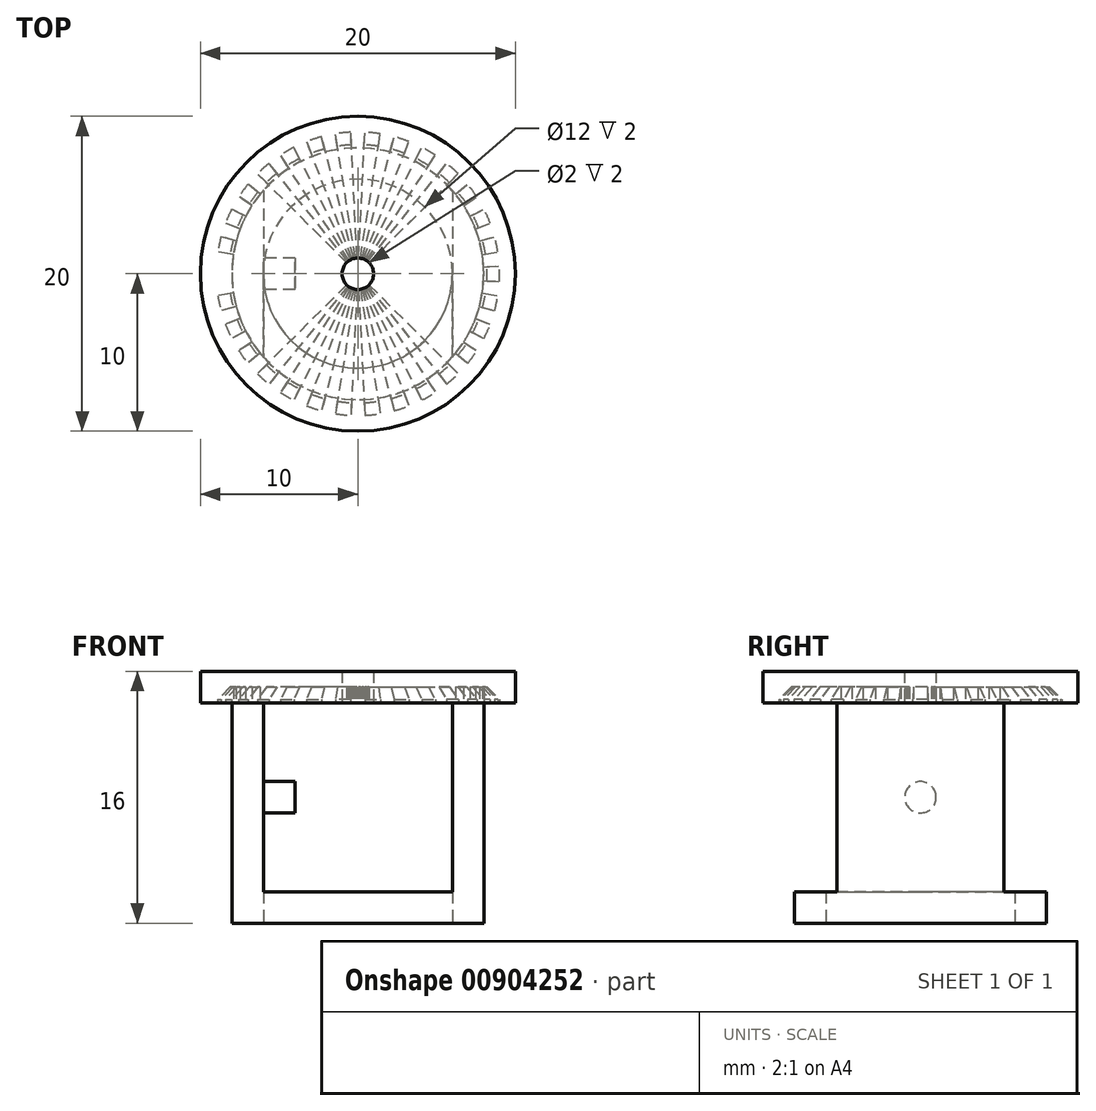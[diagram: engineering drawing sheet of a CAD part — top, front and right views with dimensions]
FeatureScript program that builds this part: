
annotation { "Feature Type Name" : "Feature", "Feature Type Description" : "" }
export const myFeature = defineFeature(function(context is Context, id is Id, definition is map)
    precondition{}
    {
        {
            var Q0;
            Q0=qCreatedBy(makeId("Front.planeOp"),FACE);
            var sketch = newSketch(context, id + "F0", { "sketchPlane" : qUnion([Q0])});
            skLineSegment(sketch, "E0.bottom", {"start": v(0, 0) * mm, "end": v(-5, 0) * mm});
            skLineSegment(sketch, "E0.top", {"start": v(0, 2) * mm, "end": v(-5, 2) * mm});
            skLineSegment(sketch, "E0.left", {"start": v(0, 0) * mm, "end": v(0, 2) * mm});
            skLineSegment(sketch, "E0.right", {"start": v(-5, 0) * mm, "end": v(-5, 2) * mm});
            skLineSegment(sketch, "E1.bottom", {"start": v(-5, 2) * mm, "end": v(-4, 2) * mm});
            skLineSegment(sketch, "E1.top", {"start": v(-5, 1) * mm, "end": v(-4, 1) * mm});
            skLineSegment(sketch, "E1.left", {"start": v(-5, 2) * mm, "end": v(-5, 1) * mm});
            skLineSegment(sketch, "E1.right", {"start": v(-4, 2) * mm, "end": v(-4, 1) * mm});
            skLineSegment(sketch, "E2.bottom", {"start": v(-4, 1) * mm, "end": v(-6, 1) * mm});
            skLineSegment(sketch, "E2.top", {"start": v(-4, 11) * mm, "end": v(-6, 11) * mm});
            skLineSegment(sketch, "E2.left", {"start": v(-4, 1) * mm, "end": v(-4, 11) * mm});
            skLineSegment(sketch, "E2.right", {"start": v(-6, 1) * mm, "end": v(-6, 11) * mm});
            skLineSegment(sketch, "E3", {"start": v(-1, 2) * mm, "end": v(-1, 0) * mm});
            skLineSegment(sketch, "E4.bottom", {"start": v(-6, 1) * mm, "end": v(-5, 1) * mm});
            skLineSegment(sketch, "E4.top", {"start": v(-6, 0) * mm, "end": v(-5, 0) * mm});
            skLineSegment(sketch, "E4.left", {"start": v(-6, 1) * mm, "end": v(-6, 0) * mm});
            skLineSegment(sketch, "E4.right", {"start": v(-5, 1) * mm, "end": v(-5, 0) * mm});
            skLineSegment(sketch, "E5.bottom", {"start": v(0, 0) * mm, "end": v(-6, 0) * mm});
            skLineSegment(sketch, "E5.top", {"start": v(0, -2) * mm, "end": v(-6, -2) * mm});
            skLineSegment(sketch, "E5.left", {"start": v(0, 0) * mm, "end": v(0, -2) * mm});
            skLineSegment(sketch, "E5.right", {"start": v(-6, 0) * mm, "end": v(-6, -2) * mm});
            skLineSegment(sketch, "E6.bottom", {"start": v(0, -2) * mm, "end": v(0, -2) * mm});
            skLineSegment(sketch, "E6.top", {"start": v(0, 0) * mm, "end": v(0, 0) * mm});
            skLineSegment(sketch, "E6.left", {"start": v(0, -2) * mm, "end": v(0, 0) * mm});
            skLineSegment(sketch, "E6.right", {"start": v(0, -2) * mm, "end": v(0, 0) * mm});
            skLineSegment(sketch, "E7.bottom", {"start": v(-6, -2) * mm, "end": v(-8, -2) * mm});
            skLineSegment(sketch, "E7.top", {"start": v(-6, 11) * mm, "end": v(-8, 11) * mm});
            skLineSegment(sketch, "E7.left", {"start": v(-6, -2) * mm, "end": v(-6, 11) * mm});
            skLineSegment(sketch, "E7.right", {"start": v(-8, -2) * mm, "end": v(-8, 11) * mm});
            skLineSegment(sketch, "E8.bottom", {"start": v(-4, 11) * mm, "end": v(-5, 11) * mm});
            skLineSegment(sketch, "E8.top", {"start": v(-4, 10) * mm, "end": v(-5, 10) * mm});
            skLineSegment(sketch, "E8.left", {"start": v(-4, 11) * mm, "end": v(-4, 10) * mm});
            skLineSegment(sketch, "E8.right", {"start": v(-5, 11) * mm, "end": v(-5, 10) * mm});
            skLineSegment(sketch, "E9.bottom", {"start": v(-5, 10) * mm, "end": v(0, 10) * mm});
            skLineSegment(sketch, "E9.top", {"start": v(-5, 12) * mm, "end": v(0, 12) * mm});
            skLineSegment(sketch, "E9.left", {"start": v(-5, 10) * mm, "end": v(-5, 12) * mm});
            skLineSegment(sketch, "E9.right", {"start": v(0, 10) * mm, "end": v(0, 12) * mm});
            skLineSegment(sketch, "E10.bottom", {"start": v(-8, 11) * mm, "end": v(-5, 11) * mm});
            skLineSegment(sketch, "E10.top", {"start": v(-8, 12) * mm, "end": v(-5, 12) * mm});
            skLineSegment(sketch, "E10.left", {"start": v(-8, 11) * mm, "end": v(-8, 12) * mm});
            skLineSegment(sketch, "E10.right", {"start": v(-5, 11) * mm, "end": v(-5, 12) * mm});
            skLineSegment(sketch, "E11", {"start": v(-6, 11) * mm, "end": v(-6, 12) * mm});
            skLineSegment(sketch, "E12.bottom", {"start": v(0, 12) * mm, "end": v(-8, 12) * mm});
            skLineSegment(sketch, "E12.top", {"start": v(0, 14) * mm, "end": v(-8, 14) * mm});
            skLineSegment(sketch, "E12.left", {"start": v(0, 12) * mm, "end": v(0, 14) * mm});
            skLineSegment(sketch, "E12.right", {"start": v(-8, 12) * mm, "end": v(-8, 14) * mm});
            skLineSegment(sketch, "E13", {"start": v(-1, 0) * mm, "end": v(-1, -2) * mm});
            skLineSegment(sketch, "E14", {"start": v(-1, -2) * mm, "end": v(-1, 14) * mm});
            skLineSegment(sketch, "E15.bottom", {"start": v(-8, 12) * mm, "end": v(-10, 12) * mm});
            skLineSegment(sketch, "E15.top", {"start": v(-8, 14) * mm, "end": v(-10, 14) * mm});
            skLineSegment(sketch, "E15.right", {"start": v(-10, 12) * mm, "end": v(-10, 14) * mm});
            skSolve(sketch);
        }
        {
            var Q0;
            {var subQ5=sQuery(id+"F0.wireOp",EDGE,"E7.bottom");Q0=makeQuery(id+"F0.imprint","IMPRINT",FACE,{"disambiguationData":[TD([[makeQuery(id+"F0.imprint","IMPRINT",EDGE,{"derivedFrom":subQ5}),-1.0]])]});}
            var Q1;
            {var subQ5=sQuery(id+"F0.wireOp",EDGE,"E5.bottom");var subQ7=makeQuery(id+"F0.imprint","INTERSECT",VERTEX,{"derivedFrom":[sQuery(id+"F0.wireOp",EDGE,"E4.right"),subQ5]});Q1=makeQuery(id+"F0.imprint","IMPRINT",FACE,{"disambiguationData":[TD([[makeQuery(id+"F0.imprint","IMPRINT",EDGE,{"disambiguationData":[TD([[subQ7,1.0]])],"derivedFrom":subQ5}),1.0]])]});}
            var Q2;
            {var subQ0=sQuery(id+"F0.wireOp",EDGE,"E12.right");Q2=makeQuery(id+"F0.imprint","IMPRINT",FACE,{"disambiguationData":[TD([[makeQuery(id+"F0.imprint","IMPRINT",EDGE,{"derivedFrom":subQ0}),-1.0]])]});}
            var Q3;
            Q3=makeQuery(id+"F0.imprint","IMPRINT",FACE,{"disambiguationData":[TD([[makeQuery(id+"F0.imprint","IMPRINT",EDGE,{"derivedFrom":sQuery(id+"F0.wireOp",EDGE,"E15.bottom")}),-1.0]])]});
            var Q4;
            {var subQ2=sQuery(id+"F0.wireOp",EDGE,"E10.left");Q4=makeQuery(id+"F0.imprint","IMPRINT",FACE,{"disambiguationData":[TD([[makeQuery(id+"F0.imprint","IMPRINT",EDGE,{"derivedFrom":subQ2}),-1.0]])]});}
            var Q5;
            Q5=sQuery(id+"F0.wireOp",EDGE,"E9.right");
            revolve(context, id + "F1", {"surfaceOperationType" : NewSurfaceOperationType.NEW, "entities" : qUnion([Q0, Q1, Q2, Q3, Q4]), "axis" : qUnion([Q5]), "revolveType" : RevolveType.FULL});
        }
        {
            var Q0;
            Q0=qCreatedBy(makeId("Front.planeOp"),FACE);
            var sketch = newSketch(context, id + "F2", { "sketchPlane" : qUnion([Q0])});
            skLineSegment(sketch, "E16.0", {"start": v(6, 0) * mm, "end": v(-6, 0) * mm});
            skLineSegment(sketch, "E17.0", {"start": v(10, 12) * mm, "end": v(-10, 12) * mm});
            skLineSegment(sketch, "E18", {"start": v(-6, 0) * mm, "end": v(-6, 12) * mm});
            skLineSegment(sketch, "E19", {"start": v(6, 0) * mm, "end": v(6, 12) * mm});
            skSolve(sketch);
        }
        {
            var Q0;
            Q0=makeQuery(id+"F2.imprint","IMPRINT",FACE,{"disambiguationData":[TD([[makeQuery(id+"F2.imprint","IMPRINT",EDGE,{"derivedFrom":sQuery(id+"F2.wireOp",EDGE,"E16.0")}),-1.0]])]});
            extrude(context, id + "F3", {"entities" : qUnion([Q0]), "operationType" : NewBodyOperationType.REMOVE, "oppositeDirection" : true, "depth" : 25 * mm, "offsetDistance" : 25 * mm});
        }
        {
            var Q0;
            Q0=makeQuery(id+"F2.imprint","IMPRINT",FACE,{"disambiguationData":[TD([[makeQuery(id+"F2.imprint","IMPRINT",EDGE,{"derivedFrom":sQuery(id+"F2.wireOp",EDGE,"E16.0")}),-1.0]])]});
            extrude(context, id + "F4", {"entities" : qUnion([Q0]), "operationType" : NewBodyOperationType.REMOVE, "oppositeDirection" : true, "depth" : -25 * mm, "offsetDistance" : 25 * mm});
        }
        {
            var Q0;
            Q0=makeQuery(id+"F1.opRevolve","SWEPT_FACE",FACE,{"disambiguationData":[OSD([sQuery(id+"F0.wireOp",EDGE,"E12.top"),sQuery(id+"F0.wireOp",EDGE,"E15.top")])]});
            var sketch = newSketch(context, id + "F5", { "sketchPlane" : qUnion([Q0])});
            skLineSegment(sketch, "E20", {"start": v(-0.5, 9.99) * mm, "end": v(0.5, 9.99) * mm});
            skLineSegment(sketch, "E21", {"start": v(0, 0) * mm, "end": v(0.5, 9.99) * mm});
            skLineSegment(sketch, "E22", {"start": v(0, 0) * mm, "end": v(-0.5, 9.99) * mm});
            skCircle(sketch, "E23", {"center": v(0, 0) * mm, "radius": 9 * mm});
            skLineSegment(sketch, "E24", {"start": v(0, 0) * mm, "end": v(9, 0) * mm});
            skLineSegment(sketch, "E25", {"start": v(9, 0) * mm, "end": v(10, 0) * mm});
            skLineSegment(sketch, "E26.1.0", {"start": v(0, 0) * mm, "end": v(-2.57, 9.67) * mm});
            skLineSegment(sketch, "E26.1.1", {"start": v(0, 0) * mm, "end": v(-1.59, 9.87) * mm});
            skLineSegment(sketch, "E26.2.0", {"start": v(0, 0) * mm, "end": v(-4.52, 8.92) * mm});
            skLineSegment(sketch, "E26.2.1", {"start": v(0, 0) * mm, "end": v(-3.6, 9.33) * mm});
            skLineSegment(sketch, "E27.2.3.0", {"start": v(0, 0) * mm, "end": v(-6.28, 7.79) * mm});
            skLineSegment(sketch, "E27.3.3.0", {"start": v(0, 0) * mm, "end": v(-5.47, 8.37) * mm});
            skLineSegment(sketch, "E27.2.4.0", {"start": v(0, 0) * mm, "end": v(-7.76, 6.31) * mm});
            skLineSegment(sketch, "E27.3.4.0", {"start": v(0, 0) * mm, "end": v(-7.09, 7.05) * mm});
            skLineSegment(sketch, "E27.2.5.0", {"start": v(0, 0) * mm, "end": v(-8.9, 4.56) * mm});
            skLineSegment(sketch, "E27.3.5.0", {"start": v(0, 0) * mm, "end": v(-8.4, 5.43) * mm});
            skLineSegment(sketch, "E27.2.6.0", {"start": v(0, 0) * mm, "end": v(-9.65, 2.61) * mm});
            skLineSegment(sketch, "E27.3.6.0", {"start": v(0, 0) * mm, "end": v(-9.34, 3.56) * mm});
            skLineSegment(sketch, "E27.2.7.0", {"start": v(0, 0) * mm, "end": v(-9.99, 0.55) * mm});
            skLineSegment(sketch, "E27.3.7.0", {"start": v(0, 0) * mm, "end": v(-9.88, 1.54) * mm});
            skLineSegment(sketch, "E27.2.8.0", {"start": v(0, 0) * mm, "end": v(-9.88, -1.54) * mm});
            skLineSegment(sketch, "E27.3.8.0", {"start": v(0, 0) * mm, "end": v(-9.99, -0.55) * mm});
            skLineSegment(sketch, "E27.2.9.0", {"start": v(0, 0) * mm, "end": v(-9.34, -3.56) * mm});
            skLineSegment(sketch, "E27.3.9.0", {"start": v(0, 0) * mm, "end": v(-9.65, -2.61) * mm});
            skLineSegment(sketch, "E27.2.10.0", {"start": v(0, 0) * mm, "end": v(-8.4, -5.43) * mm});
            skLineSegment(sketch, "E27.3.10.0", {"start": v(0, 0) * mm, "end": v(-8.9, -4.56) * mm});
            skLineSegment(sketch, "E27.2.11.0", {"start": v(0, 0) * mm, "end": v(-7.09, -7.05) * mm});
            skLineSegment(sketch, "E27.3.11.0", {"start": v(0, 0) * mm, "end": v(-7.76, -6.31) * mm});
            skLineSegment(sketch, "E27.2.12.0", {"start": v(0, 0) * mm, "end": v(-5.47, -8.37) * mm});
            skLineSegment(sketch, "E27.3.12.0", {"start": v(0, 0) * mm, "end": v(-6.28, -7.79) * mm});
            skLineSegment(sketch, "E27.2.13.0", {"start": v(0, 0) * mm, "end": v(-3.6, -9.33) * mm});
            skLineSegment(sketch, "E27.3.13.0", {"start": v(0, 0) * mm, "end": v(-4.52, -8.92) * mm});
            skLineSegment(sketch, "E27.2.14.0", {"start": v(0, 0) * mm, "end": v(-1.59, -9.87) * mm});
            skLineSegment(sketch, "E27.3.14.0", {"start": v(0, 0) * mm, "end": v(-2.57, -9.67) * mm});
            skLineSegment(sketch, "E27.2.15.0", {"start": v(0, 0) * mm, "end": v(0.5, -9.99) * mm});
            skLineSegment(sketch, "E27.3.15.0", {"start": v(0, 0) * mm, "end": v(-0.5, -9.99) * mm});
            skLineSegment(sketch, "E27.2.16.0", {"start": v(0, 0) * mm, "end": v(2.57, -9.67) * mm});
            skLineSegment(sketch, "E27.3.16.0", {"start": v(0, 0) * mm, "end": v(1.59, -9.87) * mm});
            skLineSegment(sketch, "E27.2.17.0", {"start": v(0, 0) * mm, "end": v(4.52, -8.92) * mm});
            skLineSegment(sketch, "E27.3.17.0", {"start": v(0, 0) * mm, "end": v(3.6, -9.33) * mm});
            skLineSegment(sketch, "E27.2.18.0", {"start": v(0, 0) * mm, "end": v(6.28, -7.79) * mm});
            skLineSegment(sketch, "E27.3.18.0", {"start": v(0, 0) * mm, "end": v(5.47, -8.37) * mm});
            skLineSegment(sketch, "E27.2.19.0", {"start": v(0, 0) * mm, "end": v(7.76, -6.31) * mm});
            skLineSegment(sketch, "E27.3.19.0", {"start": v(0, 0) * mm, "end": v(7.09, -7.05) * mm});
            skLineSegment(sketch, "E27.2.20.0", {"start": v(0, 0) * mm, "end": v(8.9, -4.56) * mm});
            skLineSegment(sketch, "E27.3.20.0", {"start": v(0, 0) * mm, "end": v(8.4, -5.43) * mm});
            skLineSegment(sketch, "E27.2.21.0", {"start": v(0, 0) * mm, "end": v(9.65, -2.61) * mm});
            skLineSegment(sketch, "E27.3.21.0", {"start": v(0, 0) * mm, "end": v(9.34, -3.56) * mm});
            skLineSegment(sketch, "E27.2.22.0", {"start": v(0, 0) * mm, "end": v(9.99, -0.55) * mm});
            skLineSegment(sketch, "E27.3.22.0", {"start": v(0, 0) * mm, "end": v(9.88, -1.54) * mm});
            skLineSegment(sketch, "E27.2.23.0", {"start": v(0, 0) * mm, "end": v(9.88, 1.54) * mm});
            skLineSegment(sketch, "E27.3.23.0", {"start": v(0, 0) * mm, "end": v(9.99, 0.55) * mm});
            skLineSegment(sketch, "E27.2.24.0", {"start": v(0, 0) * mm, "end": v(9.34, 3.56) * mm});
            skLineSegment(sketch, "E27.3.24.0", {"start": v(0, 0) * mm, "end": v(9.65, 2.61) * mm});
            skLineSegment(sketch, "E28.2.25.0", {"start": v(0, 0) * mm, "end": v(8.4, 5.43) * mm});
            skLineSegment(sketch, "E28.3.25.0", {"start": v(0, 0) * mm, "end": v(8.9, 4.56) * mm});
            skLineSegment(sketch, "E29.2.26.0", {"start": v(0, 0) * mm, "end": v(7.09, 7.05) * mm});
            skLineSegment(sketch, "E29.3.26.0", {"start": v(0, 0) * mm, "end": v(7.76, 6.31) * mm});
            skLineSegment(sketch, "E29.2.27.0", {"start": v(0, 0) * mm, "end": v(5.47, 8.37) * mm});
            skLineSegment(sketch, "E29.3.27.0", {"start": v(0, 0) * mm, "end": v(6.28, 7.79) * mm});
            skLineSegment(sketch, "E29.2.28.0", {"start": v(0, 0) * mm, "end": v(3.6, 9.33) * mm});
            skLineSegment(sketch, "E29.3.28.0", {"start": v(0, 0) * mm, "end": v(4.52, 8.92) * mm});
            skLineSegment(sketch, "E29.2.29.0", {"start": v(0, 0) * mm, "end": v(1.59, 9.87) * mm});
            skLineSegment(sketch, "E29.3.29.0", {"start": v(0, 0) * mm, "end": v(2.57, 9.67) * mm});
            skSolve(sketch);
        }
        {
            var Q0;
            {var subQ0=sQuery(id+"F2.wireOp",EDGE,"E18");Q0=makeQuery(id+"F4.boolean.opBoolean","MERGE",FACE,{"derivedFrom":[makeQuery(id+"F3.boolean.opBoolean","COPY",FACE,{"derivedFrom":makeQuery(id+"F3.opExtrude","SWEPT_FACE",FACE,{"disambiguationData":[OSD([subQ0])]})})],"fromTools":[makeQuery(id+"F4.opExtrude","SWEPT_FACE",FACE,{"disambiguationData":[OSD([subQ0])]})]});}
            var sketch = newSketch(context, id + "F6", { "sketchPlane" : qUnion([Q0])});
            skLineSegment(sketch, "E30.0", {"start": v(10, 12) * mm, "end": v(-10, 12) * mm});
            skLineSegment(sketch, "E31.0", {"start": v(5.3, 0) * mm, "end": v(8, 0) * mm});
            skLineSegment(sketch, "E32.0", {"start": v(-5.3, 0) * mm, "end": v(-8, 0) * mm});
            skLineSegment(sketch, "E33", {"start": v(-5.3, 0) * mm, "end": v(5.3, 0) * mm});
            skLineSegment(sketch, "E34", {"start": v(0, 0) * mm, "end": v(0, 12) * mm});
            skLineSegment(sketch, "E35.0", {"start": v(-5.3, 12) * mm, "end": v(-5.3, 0) * mm});
            skLineSegment(sketch, "E36.0", {"start": v(5.3, 12) * mm, "end": v(5.3, 0) * mm});
            skLineSegment(sketch, "E37", {"start": v(-5.3, 6) * mm, "end": v(5.3, 6) * mm});
            skCircle(sketch, "E38", {"center": v(0, 6) * mm, "radius": 1 * mm});
            skSolve(sketch);
        }
        {
            var Q0;
            {var subQ0=sQuery(id+"F6.wireOp",EDGE,"E37");var subQ1=sQuery(id+"F6.wireOp",EDGE,"E34");var subQ2=makeQuery(id+"F6.imprint","INTERSECT",VERTEX,{"derivedFrom":[subQ1,subQ0]});Q0=makeQuery(id+"F6.imprint","IMPRINT",FACE,{"disambiguationData":[TD([[makeQuery(id+"F6.imprint","IMPRINT",EDGE,{"disambiguationData":[TD([[subQ2,-1.0]])],"derivedFrom":subQ1}),-1.0]])]});}
            var Q1;
            {var subQ0=sQuery(id+"F6.wireOp",EDGE,"E38");var subQ1=sQuery(id+"F6.wireOp",EDGE,"E34");var subQ2=makeQuery(id+"F6.imprint","INTERSECT",VERTEX,{"disambiguationData":[OD(0.0)],"derivedFrom":[subQ1,subQ0]});Q1=makeQuery(id+"F6.imprint","IMPRINT",FACE,{"disambiguationData":[TD([[makeQuery(id+"F6.imprint","IMPRINT",EDGE,{"disambiguationData":[TD([[subQ2,-1.0]])],"derivedFrom":subQ1}),-1.0]])]});}
            var Q2;
            {var subQ0=sQuery(id+"F6.wireOp",EDGE,"E38");var subQ1=sQuery(id+"F6.wireOp",EDGE,"E34");var subQ2=makeQuery(id+"F6.imprint","INTERSECT",VERTEX,{"disambiguationData":[OD(0.0)],"derivedFrom":[subQ1,subQ0]});Q2=makeQuery(id+"F6.imprint","IMPRINT",FACE,{"disambiguationData":[TD([[makeQuery(id+"F6.imprint","IMPRINT",EDGE,{"disambiguationData":[TD([[subQ2,-1.0]])],"derivedFrom":subQ1}),1.0]])]});}
            var Q3;
            {var subQ0=sQuery(id+"F6.wireOp",EDGE,"E37");var subQ1=sQuery(id+"F6.wireOp",EDGE,"E34");var subQ2=makeQuery(id+"F6.imprint","INTERSECT",VERTEX,{"derivedFrom":[subQ1,subQ0]});Q3=makeQuery(id+"F6.imprint","IMPRINT",FACE,{"disambiguationData":[TD([[makeQuery(id+"F6.imprint","IMPRINT",EDGE,{"disambiguationData":[TD([[subQ2,-1.0]])],"derivedFrom":subQ1}),1.0]])]});}
            extrude(context, id + "F7", {"entities" : qUnion([Q0, Q1, Q2, Q3]), "operationType" : NewBodyOperationType.ADD, "depth" : 2 * mm, "offsetDistance" : 25 * mm});
        }
        {
            var Q0;
            {var subQ0=sQuery(id+"F2.wireOp",EDGE,"E17.0");Q0=makeQuery(id+"F4.boolean.opBoolean","MERGE",FACE,{"derivedFrom":[makeQuery(id+"F3.boolean.opBoolean","MERGE",FACE,{"derivedFrom":[makeQuery(id+"F1.opRevolve","SWEPT_FACE",FACE,{"disambiguationData":[OSD([sQuery(id+"F0.wireOp",EDGE,"E12.bottom")])]}),makeQuery(id+"F1.opRevolve","SWEPT_FACE",FACE,{"disambiguationData":[OSD([sQuery(id+"F0.wireOp",EDGE,"E15.bottom")])]})],"fromTools":[makeQuery(id+"F3.opExtrude","SWEPT_FACE",FACE,{"disambiguationData":[OSD([subQ0])]})]})],"fromTools":[makeQuery(id+"F4.opExtrude","SWEPT_FACE",FACE,{"disambiguationData":[OSD([subQ0])]})]});}
            var sketch = newSketch(context, id + "F8", { "sketchPlane" : qUnion([Q0])});
            skCircle(sketch, "E39.0", {"center": v(0, 0) * mm, "radius": 9 * mm});
            skLineSegment(sketch, "E40.0", {"start": v(0, 0) * mm, "end": v(-7.76, 6.31) * mm});
            skLineSegment(sketch, "E41.0", {"start": v(0, 0) * mm, "end": v(-7.09, 7.05) * mm});
            skLineSegment(sketch, "E42.0", {"start": v(0, 0) * mm, "end": v(-6.28, 7.79) * mm});
            skLineSegment(sketch, "E43.0", {"start": v(0, 0) * mm, "end": v(-5.47, 8.37) * mm});
            skLineSegment(sketch, "E44.0", {"start": v(0, 0) * mm, "end": v(-4.52, 8.92) * mm});
            skLineSegment(sketch, "E45.0", {"start": v(0, 0) * mm, "end": v(-3.6, 9.33) * mm});
            skLineSegment(sketch, "E46.0", {"start": v(0, 0) * mm, "end": v(-2.57, 9.67) * mm});
            skLineSegment(sketch, "E47.0", {"start": v(0, 0) * mm, "end": v(-1.59, 9.87) * mm});
            skLineSegment(sketch, "E48.0", {"start": v(0, 0) * mm, "end": v(-0.5, 9.99) * mm});
            skLineSegment(sketch, "E49.0", {"start": v(0, 0) * mm, "end": v(0.5, 9.99) * mm});
            skLineSegment(sketch, "E50.0", {"start": v(0, 0) * mm, "end": v(1.59, 9.87) * mm});
            skLineSegment(sketch, "E51.0", {"start": v(0, 0) * mm, "end": v(2.57, 9.67) * mm});
            skLineSegment(sketch, "E52.0", {"start": v(0, 0) * mm, "end": v(3.6, 9.33) * mm});
            skLineSegment(sketch, "E53.0", {"start": v(0, 0) * mm, "end": v(4.52, 8.92) * mm});
            skLineSegment(sketch, "E54.0", {"start": v(0, 0) * mm, "end": v(5.47, 8.37) * mm});
            skLineSegment(sketch, "E55.0", {"start": v(0, 0) * mm, "end": v(6.28, 7.79) * mm});
            skLineSegment(sketch, "E56.0", {"start": v(0, 0) * mm, "end": v(7.09, 7.05) * mm});
            skLineSegment(sketch, "E57.0", {"start": v(0, 0) * mm, "end": v(7.76, 6.31) * mm});
            skLineSegment(sketch, "E58.0", {"start": v(0, 0) * mm, "end": v(8.4, 5.43) * mm});
            skLineSegment(sketch, "E59.0", {"start": v(0, 0) * mm, "end": v(8.9, 4.56) * mm});
            skLineSegment(sketch, "E60.0", {"start": v(0, 0) * mm, "end": v(9.34, 3.56) * mm});
            skLineSegment(sketch, "E61.0", {"start": v(0, 0) * mm, "end": v(9.65, 2.61) * mm});
            skLineSegment(sketch, "E62.0", {"start": v(0, 0) * mm, "end": v(9.88, 1.54) * mm});
            skLineSegment(sketch, "E63.0", {"start": v(0, 0) * mm, "end": v(9.99, 0.55) * mm});
            skLineSegment(sketch, "E64.0", {"start": v(0, 0) * mm, "end": v(9.99, -0.55) * mm});
            skLineSegment(sketch, "E65.0", {"start": v(0, 0) * mm, "end": v(9.88, -1.54) * mm});
            skLineSegment(sketch, "E66.0", {"start": v(0, 0) * mm, "end": v(9.65, -2.61) * mm});
            skLineSegment(sketch, "E67.0", {"start": v(0, 0) * mm, "end": v(9.34, -3.56) * mm});
            skLineSegment(sketch, "E68.0", {"start": v(0, 0) * mm, "end": v(8.9, -4.56) * mm});
            skLineSegment(sketch, "E69.0", {"start": v(0, 0) * mm, "end": v(8.4, -5.43) * mm});
            skLineSegment(sketch, "E70.0", {"start": v(0, 0) * mm, "end": v(7.76, -6.31) * mm});
            skLineSegment(sketch, "E71.0", {"start": v(0, 0) * mm, "end": v(7.09, -7.05) * mm});
            skLineSegment(sketch, "E72.0", {"start": v(0, 0) * mm, "end": v(6.28, -7.79) * mm});
            skLineSegment(sketch, "E73.0", {"start": v(0, 0) * mm, "end": v(5.47, -8.37) * mm});
            skLineSegment(sketch, "E74.0", {"start": v(0, 0) * mm, "end": v(4.52, -8.92) * mm});
            skLineSegment(sketch, "E75.0", {"start": v(0, 0) * mm, "end": v(3.6, -9.33) * mm});
            skLineSegment(sketch, "E76.0", {"start": v(0, 0) * mm, "end": v(2.57, -9.67) * mm});
            skLineSegment(sketch, "E77.0", {"start": v(0, 0) * mm, "end": v(1.59, -9.87) * mm});
            skLineSegment(sketch, "E78.0", {"start": v(0, 0) * mm, "end": v(0.5, -9.99) * mm});
            skLineSegment(sketch, "E79.0", {"start": v(0, 0) * mm, "end": v(-0.5, -9.99) * mm});
            skLineSegment(sketch, "E80.0", {"start": v(0, 0) * mm, "end": v(-1.59, -9.87) * mm});
            skLineSegment(sketch, "E81.0", {"start": v(0, 0) * mm, "end": v(-2.57, -9.67) * mm});
            skLineSegment(sketch, "E82.0", {"start": v(0, 0) * mm, "end": v(-3.6, -9.33) * mm});
            skLineSegment(sketch, "E83.0", {"start": v(0, 0) * mm, "end": v(-4.52, -8.92) * mm});
            skLineSegment(sketch, "E84.0", {"start": v(0, 0) * mm, "end": v(-5.47, -8.37) * mm});
            skLineSegment(sketch, "E85.0", {"start": v(0, 0) * mm, "end": v(-6.28, -7.79) * mm});
            skLineSegment(sketch, "E86.0", {"start": v(0, 0) * mm, "end": v(-7.09, -7.05) * mm});
            skLineSegment(sketch, "E87.0", {"start": v(0, 0) * mm, "end": v(-7.76, -6.31) * mm});
            skLineSegment(sketch, "E88.0", {"start": v(0, 0) * mm, "end": v(-8.4, -5.43) * mm});
            skLineSegment(sketch, "E89.0", {"start": v(0, 0) * mm, "end": v(-8.9, -4.56) * mm});
            skLineSegment(sketch, "E90.0", {"start": v(0, 0) * mm, "end": v(-9.34, -3.56) * mm});
            skLineSegment(sketch, "E91.0", {"start": v(0, 0) * mm, "end": v(-9.65, -2.61) * mm});
            skLineSegment(sketch, "E92.0", {"start": v(0, 0) * mm, "end": v(-9.88, -1.54) * mm});
            skLineSegment(sketch, "E93.0", {"start": v(0, 0) * mm, "end": v(-9.99, -0.55) * mm});
            skLineSegment(sketch, "E94.0", {"start": v(0, 0) * mm, "end": v(-9.99, 0.55) * mm});
            skLineSegment(sketch, "E95.0", {"start": v(0, 0) * mm, "end": v(-9.88, 1.54) * mm});
            skLineSegment(sketch, "E96.0", {"start": v(0, 0) * mm, "end": v(-9.65, 2.61) * mm});
            skLineSegment(sketch, "E97.0", {"start": v(0, 0) * mm, "end": v(-9.34, 3.56) * mm});
            skLineSegment(sketch, "E98.0", {"start": v(0, 0) * mm, "end": v(-8.9, 4.56) * mm});
            skLineSegment(sketch, "E99.0", {"start": v(0, 0) * mm, "end": v(-8.4, 5.43) * mm});
            skSolve(sketch);
        }
        {
            var Q0;
            {var subQ0=sQuery(id+"F8.wireOp",EDGE,"E48.0");var subQ1=sQuery(id+"F8.wireOp",EDGE,"E39.0");var subQ2=makeQuery(id+"F8.imprint","INTERSECT",VERTEX,{"derivedFrom":[subQ1,subQ0]});Q0=makeQuery(id+"F8.imprint","IMPRINT",FACE,{"disambiguationData":[TD([[makeQuery(id+"F8.imprint","IMPRINT",EDGE,{"disambiguationData":[TD([[subQ2,-1.0]])],"derivedFrom":subQ1}),1.0]])]});}
            var Q1;
            {var subQ0=sQuery(id+"F8.wireOp",EDGE,"E50.0");var subQ1=sQuery(id+"F8.wireOp",EDGE,"E39.0");var subQ2=makeQuery(id+"F8.imprint","INTERSECT",VERTEX,{"derivedFrom":[subQ1,subQ0]});Q1=makeQuery(id+"F8.imprint","IMPRINT",FACE,{"disambiguationData":[TD([[makeQuery(id+"F8.imprint","IMPRINT",EDGE,{"disambiguationData":[TD([[subQ2,-1.0]])],"derivedFrom":subQ1}),1.0]])]});}
            var Q2;
            {var subQ0=sQuery(id+"F8.wireOp",EDGE,"E52.0");var subQ1=sQuery(id+"F8.wireOp",EDGE,"E39.0");var subQ2=makeQuery(id+"F8.imprint","INTERSECT",VERTEX,{"derivedFrom":[subQ1,subQ0]});Q2=makeQuery(id+"F8.imprint","IMPRINT",FACE,{"disambiguationData":[TD([[makeQuery(id+"F8.imprint","IMPRINT",EDGE,{"disambiguationData":[TD([[subQ2,-1.0]])],"derivedFrom":subQ1}),1.0]])]});}
            var Q3;
            {var subQ0=sQuery(id+"F8.wireOp",EDGE,"E54.0");var subQ1=sQuery(id+"F8.wireOp",EDGE,"E39.0");var subQ2=makeQuery(id+"F8.imprint","INTERSECT",VERTEX,{"derivedFrom":[subQ1,subQ0]});Q3=makeQuery(id+"F8.imprint","IMPRINT",FACE,{"disambiguationData":[TD([[makeQuery(id+"F8.imprint","IMPRINT",EDGE,{"disambiguationData":[TD([[subQ2,-1.0]])],"derivedFrom":subQ1}),1.0]])]});}
            var Q4;
            {var subQ0=sQuery(id+"F8.wireOp",EDGE,"E56.0");var subQ1=sQuery(id+"F8.wireOp",EDGE,"E39.0");var subQ2=makeQuery(id+"F8.imprint","INTERSECT",VERTEX,{"derivedFrom":[subQ1,subQ0]});Q4=makeQuery(id+"F8.imprint","IMPRINT",FACE,{"disambiguationData":[TD([[makeQuery(id+"F8.imprint","IMPRINT",EDGE,{"disambiguationData":[TD([[subQ2,-1.0]])],"derivedFrom":subQ1}),1.0]])]});}
            var Q5;
            {var subQ0=sQuery(id+"F8.wireOp",EDGE,"E58.0");var subQ1=sQuery(id+"F8.wireOp",EDGE,"E39.0");var subQ2=makeQuery(id+"F8.imprint","INTERSECT",VERTEX,{"derivedFrom":[subQ1,subQ0]});Q5=makeQuery(id+"F8.imprint","IMPRINT",FACE,{"disambiguationData":[TD([[makeQuery(id+"F8.imprint","IMPRINT",EDGE,{"disambiguationData":[TD([[subQ2,-1.0]])],"derivedFrom":subQ1}),1.0]])]});}
            var Q6;
            {var subQ0=sQuery(id+"F8.wireOp",EDGE,"E60.0");var subQ1=sQuery(id+"F8.wireOp",EDGE,"E39.0");var subQ2=makeQuery(id+"F8.imprint","INTERSECT",VERTEX,{"derivedFrom":[subQ1,subQ0]});Q6=makeQuery(id+"F8.imprint","IMPRINT",FACE,{"disambiguationData":[TD([[makeQuery(id+"F8.imprint","IMPRINT",EDGE,{"disambiguationData":[TD([[subQ2,-1.0]])],"derivedFrom":subQ1}),1.0]])]});}
            var Q7;
            {var subQ0=sQuery(id+"F8.wireOp",EDGE,"E62.0");var subQ1=sQuery(id+"F8.wireOp",EDGE,"E39.0");var subQ2=makeQuery(id+"F8.imprint","INTERSECT",VERTEX,{"derivedFrom":[subQ1,subQ0]});Q7=makeQuery(id+"F8.imprint","IMPRINT",FACE,{"disambiguationData":[TD([[makeQuery(id+"F8.imprint","IMPRINT",EDGE,{"disambiguationData":[TD([[subQ2,-1.0]])],"derivedFrom":subQ1}),1.0]])]});}
            var Q8;
            {var subQ0=sQuery(id+"F8.wireOp",EDGE,"E64.0");var subQ1=sQuery(id+"F8.wireOp",EDGE,"E39.0");var subQ2=makeQuery(id+"F8.imprint","INTERSECT",VERTEX,{"derivedFrom":[subQ1,subQ0]});Q8=makeQuery(id+"F8.imprint","IMPRINT",FACE,{"disambiguationData":[TD([[makeQuery(id+"F8.imprint","IMPRINT",EDGE,{"disambiguationData":[TD([[subQ2,-1.0]])],"derivedFrom":subQ1}),1.0]])]});}
            var Q9;
            {var subQ0=sQuery(id+"F8.wireOp",EDGE,"E66.0");var subQ1=sQuery(id+"F8.wireOp",EDGE,"E39.0");var subQ2=makeQuery(id+"F8.imprint","INTERSECT",VERTEX,{"derivedFrom":[subQ1,subQ0]});Q9=makeQuery(id+"F8.imprint","IMPRINT",FACE,{"disambiguationData":[TD([[makeQuery(id+"F8.imprint","IMPRINT",EDGE,{"disambiguationData":[TD([[subQ2,-1.0]])],"derivedFrom":subQ1}),1.0]])]});}
            var Q10;
            {var subQ0=sQuery(id+"F8.wireOp",EDGE,"E68.0");var subQ1=sQuery(id+"F8.wireOp",EDGE,"E39.0");var subQ2=makeQuery(id+"F8.imprint","INTERSECT",VERTEX,{"derivedFrom":[subQ1,subQ0]});Q10=makeQuery(id+"F8.imprint","IMPRINT",FACE,{"disambiguationData":[TD([[makeQuery(id+"F8.imprint","IMPRINT",EDGE,{"disambiguationData":[TD([[subQ2,-1.0]])],"derivedFrom":subQ1}),1.0]])]});}
            var Q11;
            {var subQ0=sQuery(id+"F8.wireOp",EDGE,"E70.0");var subQ1=sQuery(id+"F8.wireOp",EDGE,"E39.0");var subQ2=makeQuery(id+"F8.imprint","INTERSECT",VERTEX,{"derivedFrom":[subQ1,subQ0]});Q11=makeQuery(id+"F8.imprint","IMPRINT",FACE,{"disambiguationData":[TD([[makeQuery(id+"F8.imprint","IMPRINT",EDGE,{"disambiguationData":[TD([[subQ2,-1.0]])],"derivedFrom":subQ1}),1.0]])]});}
            var Q12;
            {var subQ0=sQuery(id+"F8.wireOp",EDGE,"E72.0");var subQ1=sQuery(id+"F8.wireOp",EDGE,"E39.0");var subQ2=makeQuery(id+"F8.imprint","INTERSECT",VERTEX,{"derivedFrom":[subQ1,subQ0]});Q12=makeQuery(id+"F8.imprint","IMPRINT",FACE,{"disambiguationData":[TD([[makeQuery(id+"F8.imprint","IMPRINT",EDGE,{"disambiguationData":[TD([[subQ2,-1.0]])],"derivedFrom":subQ1}),1.0]])]});}
            var Q13;
            {var subQ0=sQuery(id+"F8.wireOp",EDGE,"E46.0");var subQ1=sQuery(id+"F8.wireOp",EDGE,"E39.0");var subQ2=makeQuery(id+"F8.imprint","INTERSECT",VERTEX,{"derivedFrom":[subQ1,subQ0]});Q13=makeQuery(id+"F8.imprint","IMPRINT",FACE,{"disambiguationData":[TD([[makeQuery(id+"F8.imprint","IMPRINT",EDGE,{"disambiguationData":[TD([[subQ2,-1.0]])],"derivedFrom":subQ1}),1.0]])]});}
            var Q14;
            {var subQ0=sQuery(id+"F8.wireOp",EDGE,"E44.0");var subQ1=sQuery(id+"F8.wireOp",EDGE,"E39.0");var subQ2=makeQuery(id+"F8.imprint","INTERSECT",VERTEX,{"derivedFrom":[subQ1,subQ0]});Q14=makeQuery(id+"F8.imprint","IMPRINT",FACE,{"disambiguationData":[TD([[makeQuery(id+"F8.imprint","IMPRINT",EDGE,{"disambiguationData":[TD([[subQ2,-1.0]])],"derivedFrom":subQ1}),1.0]])]});}
            var Q15;
            {var subQ0=sQuery(id+"F8.wireOp",EDGE,"E42.0");var subQ1=sQuery(id+"F8.wireOp",EDGE,"E39.0");var subQ2=makeQuery(id+"F8.imprint","INTERSECT",VERTEX,{"derivedFrom":[subQ1,subQ0]});Q15=makeQuery(id+"F8.imprint","IMPRINT",FACE,{"disambiguationData":[TD([[makeQuery(id+"F8.imprint","IMPRINT",EDGE,{"disambiguationData":[TD([[subQ2,-1.0]])],"derivedFrom":subQ1}),1.0]])]});}
            var Q16;
            {var subQ0=sQuery(id+"F8.wireOp",EDGE,"E40.0");var subQ1=sQuery(id+"F8.wireOp",EDGE,"E39.0");var subQ2=makeQuery(id+"F8.imprint","INTERSECT",VERTEX,{"derivedFrom":[subQ1,subQ0]});Q16=makeQuery(id+"F8.imprint","IMPRINT",FACE,{"disambiguationData":[TD([[makeQuery(id+"F8.imprint","IMPRINT",EDGE,{"disambiguationData":[TD([[subQ2,-1.0]])],"derivedFrom":subQ1}),1.0]])]});}
            var Q17;
            {var subQ0=sQuery(id+"F8.wireOp",EDGE,"E98.0");var subQ1=sQuery(id+"F8.wireOp",EDGE,"E39.0");var subQ2=makeQuery(id+"F8.imprint","INTERSECT",VERTEX,{"derivedFrom":[subQ1,subQ0]});Q17=makeQuery(id+"F8.imprint","IMPRINT",FACE,{"disambiguationData":[TD([[makeQuery(id+"F8.imprint","IMPRINT",EDGE,{"disambiguationData":[TD([[subQ2,-1.0]])],"derivedFrom":subQ1}),1.0]])]});}
            var Q18;
            {var subQ0=sQuery(id+"F8.wireOp",EDGE,"E96.0");var subQ1=sQuery(id+"F8.wireOp",EDGE,"E39.0");var subQ2=makeQuery(id+"F8.imprint","INTERSECT",VERTEX,{"derivedFrom":[subQ1,subQ0]});Q18=makeQuery(id+"F8.imprint","IMPRINT",FACE,{"disambiguationData":[TD([[makeQuery(id+"F8.imprint","IMPRINT",EDGE,{"disambiguationData":[TD([[subQ2,-1.0]])],"derivedFrom":subQ1}),1.0]])]});}
            var Q19;
            {var subQ0=sQuery(id+"F8.wireOp",EDGE,"E95.0");var subQ1=sQuery(id+"F8.wireOp",EDGE,"E39.0");var subQ2=makeQuery(id+"F8.imprint","INTERSECT",VERTEX,{"derivedFrom":[subQ1,subQ0]});Q19=makeQuery(id+"F8.imprint","IMPRINT",FACE,{"disambiguationData":[TD([[makeQuery(id+"F8.imprint","IMPRINT",EDGE,{"disambiguationData":[TD([[subQ2,1.0]])],"derivedFrom":subQ1}),1.0]])]});}
            var Q20;
            {var subQ0=sQuery(id+"F8.wireOp",EDGE,"E92.0");var subQ1=sQuery(id+"F8.wireOp",EDGE,"E39.0");var subQ2=makeQuery(id+"F8.imprint","INTERSECT",VERTEX,{"derivedFrom":[subQ1,subQ0]});Q20=makeQuery(id+"F8.imprint","IMPRINT",FACE,{"disambiguationData":[TD([[makeQuery(id+"F8.imprint","IMPRINT",EDGE,{"disambiguationData":[TD([[subQ2,-1.0]])],"derivedFrom":subQ1}),1.0]])]});}
            var Q21;
            {var subQ0=sQuery(id+"F8.wireOp",EDGE,"E90.0");var subQ1=sQuery(id+"F8.wireOp",EDGE,"E39.0");var subQ2=makeQuery(id+"F8.imprint","INTERSECT",VERTEX,{"derivedFrom":[subQ1,subQ0]});Q21=makeQuery(id+"F8.imprint","IMPRINT",FACE,{"disambiguationData":[TD([[makeQuery(id+"F8.imprint","IMPRINT",EDGE,{"disambiguationData":[TD([[subQ2,-1.0]])],"derivedFrom":subQ1}),1.0]])]});}
            var Q22;
            {var subQ0=sQuery(id+"F8.wireOp",EDGE,"E88.0");var subQ1=sQuery(id+"F8.wireOp",EDGE,"E39.0");var subQ2=makeQuery(id+"F8.imprint","INTERSECT",VERTEX,{"derivedFrom":[subQ1,subQ0]});Q22=makeQuery(id+"F8.imprint","IMPRINT",FACE,{"disambiguationData":[TD([[makeQuery(id+"F8.imprint","IMPRINT",EDGE,{"disambiguationData":[TD([[subQ2,-1.0]])],"derivedFrom":subQ1}),1.0]])]});}
            var Q23;
            {var subQ0=sQuery(id+"F8.wireOp",EDGE,"E86.0");var subQ1=sQuery(id+"F8.wireOp",EDGE,"E39.0");var subQ2=makeQuery(id+"F8.imprint","INTERSECT",VERTEX,{"derivedFrom":[subQ1,subQ0]});Q23=makeQuery(id+"F8.imprint","IMPRINT",FACE,{"disambiguationData":[TD([[makeQuery(id+"F8.imprint","IMPRINT",EDGE,{"disambiguationData":[TD([[subQ2,-1.0]])],"derivedFrom":subQ1}),1.0]])]});}
            var Q24;
            {var subQ0=sQuery(id+"F8.wireOp",EDGE,"E74.0");var subQ1=sQuery(id+"F8.wireOp",EDGE,"E39.0");var subQ2=makeQuery(id+"F8.imprint","INTERSECT",VERTEX,{"derivedFrom":[subQ1,subQ0]});Q24=makeQuery(id+"F8.imprint","IMPRINT",FACE,{"disambiguationData":[TD([[makeQuery(id+"F8.imprint","IMPRINT",EDGE,{"disambiguationData":[TD([[subQ2,-1.0]])],"derivedFrom":subQ1}),1.0]])]});}
            var Q25;
            {var subQ0=sQuery(id+"F8.wireOp",EDGE,"E76.0");var subQ1=sQuery(id+"F8.wireOp",EDGE,"E39.0");var subQ2=makeQuery(id+"F8.imprint","INTERSECT",VERTEX,{"derivedFrom":[subQ1,subQ0]});Q25=makeQuery(id+"F8.imprint","IMPRINT",FACE,{"disambiguationData":[TD([[makeQuery(id+"F8.imprint","IMPRINT",EDGE,{"disambiguationData":[TD([[subQ2,-1.0]])],"derivedFrom":subQ1}),1.0]])]});}
            var Q26;
            {var subQ0=sQuery(id+"F8.wireOp",EDGE,"E78.0");var subQ1=sQuery(id+"F8.wireOp",EDGE,"E39.0");var subQ2=makeQuery(id+"F8.imprint","INTERSECT",VERTEX,{"derivedFrom":[subQ1,subQ0]});Q26=makeQuery(id+"F8.imprint","IMPRINT",FACE,{"disambiguationData":[TD([[makeQuery(id+"F8.imprint","IMPRINT",EDGE,{"disambiguationData":[TD([[subQ2,-1.0]])],"derivedFrom":subQ1}),1.0]])]});}
            var Q27;
            {var subQ0=sQuery(id+"F8.wireOp",EDGE,"E80.0");var subQ1=sQuery(id+"F8.wireOp",EDGE,"E39.0");var subQ2=makeQuery(id+"F8.imprint","INTERSECT",VERTEX,{"derivedFrom":[subQ1,subQ0]});Q27=makeQuery(id+"F8.imprint","IMPRINT",FACE,{"disambiguationData":[TD([[makeQuery(id+"F8.imprint","IMPRINT",EDGE,{"disambiguationData":[TD([[subQ2,-1.0]])],"derivedFrom":subQ1}),1.0]])]});}
            var Q28;
            {var subQ0=sQuery(id+"F8.wireOp",EDGE,"E82.0");var subQ1=sQuery(id+"F8.wireOp",EDGE,"E39.0");var subQ2=makeQuery(id+"F8.imprint","INTERSECT",VERTEX,{"derivedFrom":[subQ1,subQ0]});Q28=makeQuery(id+"F8.imprint","IMPRINT",FACE,{"disambiguationData":[TD([[makeQuery(id+"F8.imprint","IMPRINT",EDGE,{"disambiguationData":[TD([[subQ2,-1.0]])],"derivedFrom":subQ1}),1.0]])]});}
            var Q29;
            {var subQ0=sQuery(id+"F8.wireOp",EDGE,"E84.0");var subQ1=sQuery(id+"F8.wireOp",EDGE,"E39.0");var subQ2=makeQuery(id+"F8.imprint","INTERSECT",VERTEX,{"derivedFrom":[subQ1,subQ0]});Q29=makeQuery(id+"F8.imprint","IMPRINT",FACE,{"disambiguationData":[TD([[makeQuery(id+"F8.imprint","IMPRINT",EDGE,{"disambiguationData":[TD([[subQ2,-1.0]])],"derivedFrom":subQ1}),1.0]])]});}
            extrude(context, id + "F9", {"entities" : qUnion([Q0, Q1, Q2, Q3, Q4, Q5, Q6, Q7, Q8, Q9, Q10, Q11, Q12, Q13, Q14, Q15, Q16, Q17, Q18, Q19, Q20, Q21, Q22, Q23, Q24, Q25, Q26, Q27, Q28, Q29]), "operationType" : NewBodyOperationType.REMOVE, "oppositeDirection" : true, "depth" : 1 * mm, "offsetDistance" : 25 * mm});
        }
        {
            var Q0;
            {var subQ0=sQuery(id+"F8.wireOp",EDGE,"E39.0");Q0=makeQuery(id+"F9.boolean.opBoolean","COPY",EDGE,{"derivedFrom":makeQuery(id+"F9.opExtrude","CAP_EDGE",EDGE,{"disambiguationData":[OSD([subQ0]),TDD([makeQuery(id+"F8.imprint","IMPRINT",EDGE,{"disambiguationData":[TD([[makeQuery(id+"F8.imprint","INTERSECT",VERTEX,{"derivedFrom":[subQ0,sQuery(id+"F8.wireOp",EDGE,"E82.0")]}),-1.0]])],"derivedFrom":subQ0})])],"isStart":false})});}
            var Q1;
            {var subQ0=sQuery(id+"F8.wireOp",EDGE,"E39.0");Q1=makeQuery(id+"F9.boolean.opBoolean","COPY",EDGE,{"derivedFrom":makeQuery(id+"F9.opExtrude","CAP_EDGE",EDGE,{"disambiguationData":[OSD([subQ0]),TDD([makeQuery(id+"F8.imprint","IMPRINT",EDGE,{"disambiguationData":[TD([[makeQuery(id+"F8.imprint","INTERSECT",VERTEX,{"derivedFrom":[subQ0,sQuery(id+"F8.wireOp",EDGE,"E84.0")]}),-1.0]])],"derivedFrom":subQ0})])],"isStart":false})});}
            var Q2;
            {var subQ0=sQuery(id+"F8.wireOp",EDGE,"E39.0");Q2=makeQuery(id+"F9.boolean.opBoolean","COPY",EDGE,{"derivedFrom":makeQuery(id+"F9.opExtrude","CAP_EDGE",EDGE,{"disambiguationData":[OSD([subQ0]),TDD([makeQuery(id+"F8.imprint","IMPRINT",EDGE,{"disambiguationData":[TD([[makeQuery(id+"F8.imprint","INTERSECT",VERTEX,{"derivedFrom":[subQ0,sQuery(id+"F8.wireOp",EDGE,"E86.0")]}),-1.0]])],"derivedFrom":subQ0})])],"isStart":false})});}
            var Q3;
            {var subQ0=sQuery(id+"F8.wireOp",EDGE,"E39.0");Q3=makeQuery(id+"F9.boolean.opBoolean","COPY",EDGE,{"derivedFrom":makeQuery(id+"F9.opExtrude","CAP_EDGE",EDGE,{"disambiguationData":[OSD([subQ0]),TDD([makeQuery(id+"F8.imprint","IMPRINT",EDGE,{"disambiguationData":[TD([[makeQuery(id+"F8.imprint","INTERSECT",VERTEX,{"derivedFrom":[subQ0,sQuery(id+"F8.wireOp",EDGE,"E88.0")]}),-1.0]])],"derivedFrom":subQ0})])],"isStart":false})});}
            var Q4;
            {var subQ0=sQuery(id+"F8.wireOp",EDGE,"E39.0");Q4=makeQuery(id+"F9.boolean.opBoolean","COPY",EDGE,{"derivedFrom":makeQuery(id+"F9.opExtrude","CAP_EDGE",EDGE,{"disambiguationData":[OSD([subQ0]),TDD([makeQuery(id+"F8.imprint","IMPRINT",EDGE,{"disambiguationData":[TD([[makeQuery(id+"F8.imprint","INTERSECT",VERTEX,{"derivedFrom":[subQ0,sQuery(id+"F8.wireOp",EDGE,"E90.0")]}),-1.0]])],"derivedFrom":subQ0})])],"isStart":false})});}
            var Q5;
            {var subQ0=sQuery(id+"F8.wireOp",EDGE,"E39.0");Q5=makeQuery(id+"F9.boolean.opBoolean","COPY",EDGE,{"derivedFrom":makeQuery(id+"F9.opExtrude","CAP_EDGE",EDGE,{"disambiguationData":[OSD([subQ0]),TDD([makeQuery(id+"F8.imprint","IMPRINT",EDGE,{"disambiguationData":[TD([[makeQuery(id+"F8.imprint","INTERSECT",VERTEX,{"derivedFrom":[subQ0,sQuery(id+"F8.wireOp",EDGE,"E92.0")]}),-1.0]])],"derivedFrom":subQ0})])],"isStart":false})});}
            var Q6;
            {var subQ0=sQuery(id+"F8.wireOp",EDGE,"E39.0");Q6=makeQuery(id+"F9.boolean.opBoolean","COPY",EDGE,{"derivedFrom":makeQuery(id+"F9.opExtrude","CAP_EDGE",EDGE,{"disambiguationData":[OSD([subQ0]),TDD([makeQuery(id+"F8.imprint","IMPRINT",EDGE,{"disambiguationData":[TD([[makeQuery(id+"F8.imprint","INTERSECT",VERTEX,{"derivedFrom":[subQ0,sQuery(id+"F8.wireOp",EDGE,"E95.0")]}),1.0]])],"derivedFrom":subQ0})])],"isStart":false})});}
            var Q7;
            {var subQ0=sQuery(id+"F8.wireOp",EDGE,"E39.0");Q7=makeQuery(id+"F9.boolean.opBoolean","COPY",EDGE,{"derivedFrom":makeQuery(id+"F9.opExtrude","CAP_EDGE",EDGE,{"disambiguationData":[OSD([subQ0]),TDD([makeQuery(id+"F8.imprint","IMPRINT",EDGE,{"disambiguationData":[TD([[makeQuery(id+"F8.imprint","INTERSECT",VERTEX,{"derivedFrom":[subQ0,sQuery(id+"F8.wireOp",EDGE,"E96.0")]}),-1.0]])],"derivedFrom":subQ0})])],"isStart":false})});}
            var Q8;
            {var subQ0=sQuery(id+"F8.wireOp",EDGE,"E39.0");Q8=makeQuery(id+"F9.boolean.opBoolean","COPY",EDGE,{"derivedFrom":makeQuery(id+"F9.opExtrude","CAP_EDGE",EDGE,{"disambiguationData":[OSD([subQ0]),TDD([makeQuery(id+"F8.imprint","IMPRINT",EDGE,{"disambiguationData":[TD([[makeQuery(id+"F8.imprint","INTERSECT",VERTEX,{"derivedFrom":[subQ0,sQuery(id+"F8.wireOp",EDGE,"E98.0")]}),-1.0]])],"derivedFrom":subQ0})])],"isStart":false})});}
            var Q9;
            {var subQ0=sQuery(id+"F8.wireOp",EDGE,"E39.0");Q9=makeQuery(id+"F9.boolean.opBoolean","COPY",EDGE,{"derivedFrom":makeQuery(id+"F9.opExtrude","CAP_EDGE",EDGE,{"disambiguationData":[OSD([subQ0]),TDD([makeQuery(id+"F8.imprint","IMPRINT",EDGE,{"disambiguationData":[TD([[makeQuery(id+"F8.imprint","INTERSECT",VERTEX,{"derivedFrom":[subQ0,sQuery(id+"F8.wireOp",EDGE,"E40.0")]}),-1.0]])],"derivedFrom":subQ0})])],"isStart":false})});}
            var Q10;
            {var subQ0=sQuery(id+"F8.wireOp",EDGE,"E39.0");Q10=makeQuery(id+"F9.boolean.opBoolean","COPY",EDGE,{"derivedFrom":makeQuery(id+"F9.opExtrude","CAP_EDGE",EDGE,{"disambiguationData":[OSD([subQ0]),TDD([makeQuery(id+"F8.imprint","IMPRINT",EDGE,{"disambiguationData":[TD([[makeQuery(id+"F8.imprint","INTERSECT",VERTEX,{"derivedFrom":[subQ0,sQuery(id+"F8.wireOp",EDGE,"E42.0")]}),-1.0]])],"derivedFrom":subQ0})])],"isStart":false})});}
            var Q11;
            {var subQ0=sQuery(id+"F8.wireOp",EDGE,"E39.0");Q11=makeQuery(id+"F9.boolean.opBoolean","COPY",EDGE,{"derivedFrom":makeQuery(id+"F9.opExtrude","CAP_EDGE",EDGE,{"disambiguationData":[OSD([subQ0]),TDD([makeQuery(id+"F8.imprint","IMPRINT",EDGE,{"disambiguationData":[TD([[makeQuery(id+"F8.imprint","INTERSECT",VERTEX,{"derivedFrom":[subQ0,sQuery(id+"F8.wireOp",EDGE,"E44.0")]}),-1.0]])],"derivedFrom":subQ0})])],"isStart":false})});}
            var Q12;
            {var subQ0=sQuery(id+"F8.wireOp",EDGE,"E39.0");Q12=makeQuery(id+"F9.boolean.opBoolean","COPY",EDGE,{"derivedFrom":makeQuery(id+"F9.opExtrude","CAP_EDGE",EDGE,{"disambiguationData":[OSD([subQ0]),TDD([makeQuery(id+"F8.imprint","IMPRINT",EDGE,{"disambiguationData":[TD([[makeQuery(id+"F8.imprint","INTERSECT",VERTEX,{"derivedFrom":[subQ0,sQuery(id+"F8.wireOp",EDGE,"E46.0")]}),-1.0]])],"derivedFrom":subQ0})])],"isStart":false})});}
            var Q13;
            {var subQ0=sQuery(id+"F8.wireOp",EDGE,"E39.0");Q13=makeQuery(id+"F9.boolean.opBoolean","COPY",EDGE,{"derivedFrom":makeQuery(id+"F9.opExtrude","CAP_EDGE",EDGE,{"disambiguationData":[OSD([subQ0]),TDD([makeQuery(id+"F8.imprint","IMPRINT",EDGE,{"disambiguationData":[TD([[makeQuery(id+"F8.imprint","INTERSECT",VERTEX,{"derivedFrom":[subQ0,sQuery(id+"F8.wireOp",EDGE,"E48.0")]}),-1.0]])],"derivedFrom":subQ0})])],"isStart":false})});}
            var Q14;
            {var subQ0=sQuery(id+"F8.wireOp",EDGE,"E39.0");Q14=makeQuery(id+"F9.boolean.opBoolean","COPY",EDGE,{"derivedFrom":makeQuery(id+"F9.opExtrude","CAP_EDGE",EDGE,{"disambiguationData":[OSD([subQ0]),TDD([makeQuery(id+"F8.imprint","IMPRINT",EDGE,{"disambiguationData":[TD([[makeQuery(id+"F8.imprint","INTERSECT",VERTEX,{"derivedFrom":[subQ0,sQuery(id+"F8.wireOp",EDGE,"E50.0")]}),-1.0]])],"derivedFrom":subQ0})])],"isStart":false})});}
            var Q15;
            {var subQ0=sQuery(id+"F8.wireOp",EDGE,"E39.0");Q15=makeQuery(id+"F9.boolean.opBoolean","COPY",EDGE,{"derivedFrom":makeQuery(id+"F9.opExtrude","CAP_EDGE",EDGE,{"disambiguationData":[OSD([subQ0]),TDD([makeQuery(id+"F8.imprint","IMPRINT",EDGE,{"disambiguationData":[TD([[makeQuery(id+"F8.imprint","INTERSECT",VERTEX,{"derivedFrom":[subQ0,sQuery(id+"F8.wireOp",EDGE,"E52.0")]}),-1.0]])],"derivedFrom":subQ0})])],"isStart":false})});}
            var Q16;
            {var subQ0=sQuery(id+"F8.wireOp",EDGE,"E39.0");Q16=makeQuery(id+"F9.boolean.opBoolean","COPY",EDGE,{"derivedFrom":makeQuery(id+"F9.opExtrude","CAP_EDGE",EDGE,{"disambiguationData":[OSD([subQ0]),TDD([makeQuery(id+"F8.imprint","IMPRINT",EDGE,{"disambiguationData":[TD([[makeQuery(id+"F8.imprint","INTERSECT",VERTEX,{"derivedFrom":[subQ0,sQuery(id+"F8.wireOp",EDGE,"E54.0")]}),-1.0]])],"derivedFrom":subQ0})])],"isStart":false})});}
            var Q17;
            {var subQ0=sQuery(id+"F8.wireOp",EDGE,"E39.0");Q17=makeQuery(id+"F9.boolean.opBoolean","COPY",EDGE,{"derivedFrom":makeQuery(id+"F9.opExtrude","CAP_EDGE",EDGE,{"disambiguationData":[OSD([subQ0]),TDD([makeQuery(id+"F8.imprint","IMPRINT",EDGE,{"disambiguationData":[TD([[makeQuery(id+"F8.imprint","INTERSECT",VERTEX,{"derivedFrom":[subQ0,sQuery(id+"F8.wireOp",EDGE,"E56.0")]}),-1.0]])],"derivedFrom":subQ0})])],"isStart":false})});}
            var Q18;
            {var subQ0=sQuery(id+"F8.wireOp",EDGE,"E39.0");Q18=makeQuery(id+"F9.boolean.opBoolean","COPY",EDGE,{"derivedFrom":makeQuery(id+"F9.opExtrude","CAP_EDGE",EDGE,{"disambiguationData":[OSD([subQ0]),TDD([makeQuery(id+"F8.imprint","IMPRINT",EDGE,{"disambiguationData":[TD([[makeQuery(id+"F8.imprint","INTERSECT",VERTEX,{"derivedFrom":[subQ0,sQuery(id+"F8.wireOp",EDGE,"E58.0")]}),-1.0]])],"derivedFrom":subQ0})])],"isStart":false})});}
            var Q19;
            {var subQ0=sQuery(id+"F8.wireOp",EDGE,"E39.0");Q19=makeQuery(id+"F9.boolean.opBoolean","COPY",EDGE,{"derivedFrom":makeQuery(id+"F9.opExtrude","CAP_EDGE",EDGE,{"disambiguationData":[OSD([subQ0]),TDD([makeQuery(id+"F8.imprint","IMPRINT",EDGE,{"disambiguationData":[TD([[makeQuery(id+"F8.imprint","INTERSECT",VERTEX,{"derivedFrom":[subQ0,sQuery(id+"F8.wireOp",EDGE,"E60.0")]}),-1.0]])],"derivedFrom":subQ0})])],"isStart":false})});}
            var Q20;
            {var subQ0=sQuery(id+"F8.wireOp",EDGE,"E39.0");Q20=makeQuery(id+"F9.boolean.opBoolean","COPY",EDGE,{"derivedFrom":makeQuery(id+"F9.opExtrude","CAP_EDGE",EDGE,{"disambiguationData":[OSD([subQ0]),TDD([makeQuery(id+"F8.imprint","IMPRINT",EDGE,{"disambiguationData":[TD([[makeQuery(id+"F8.imprint","INTERSECT",VERTEX,{"derivedFrom":[subQ0,sQuery(id+"F8.wireOp",EDGE,"E62.0")]}),-1.0]])],"derivedFrom":subQ0})])],"isStart":false})});}
            var Q21;
            {var subQ0=sQuery(id+"F8.wireOp",EDGE,"E39.0");Q21=makeQuery(id+"F9.boolean.opBoolean","COPY",EDGE,{"derivedFrom":makeQuery(id+"F9.opExtrude","CAP_EDGE",EDGE,{"disambiguationData":[OSD([subQ0]),TDD([makeQuery(id+"F8.imprint","IMPRINT",EDGE,{"disambiguationData":[TD([[makeQuery(id+"F8.imprint","INTERSECT",VERTEX,{"derivedFrom":[subQ0,sQuery(id+"F8.wireOp",EDGE,"E64.0")]}),-1.0]])],"derivedFrom":subQ0})])],"isStart":false})});}
            var Q22;
            {var subQ0=sQuery(id+"F8.wireOp",EDGE,"E39.0");Q22=makeQuery(id+"F9.boolean.opBoolean","COPY",EDGE,{"derivedFrom":makeQuery(id+"F9.opExtrude","CAP_EDGE",EDGE,{"disambiguationData":[OSD([subQ0]),TDD([makeQuery(id+"F8.imprint","IMPRINT",EDGE,{"disambiguationData":[TD([[makeQuery(id+"F8.imprint","INTERSECT",VERTEX,{"derivedFrom":[subQ0,sQuery(id+"F8.wireOp",EDGE,"E66.0")]}),-1.0]])],"derivedFrom":subQ0})])],"isStart":false})});}
            var Q23;
            {var subQ0=sQuery(id+"F8.wireOp",EDGE,"E39.0");Q23=makeQuery(id+"F9.boolean.opBoolean","COPY",EDGE,{"derivedFrom":makeQuery(id+"F9.opExtrude","CAP_EDGE",EDGE,{"disambiguationData":[OSD([subQ0]),TDD([makeQuery(id+"F8.imprint","IMPRINT",EDGE,{"disambiguationData":[TD([[makeQuery(id+"F8.imprint","INTERSECT",VERTEX,{"derivedFrom":[subQ0,sQuery(id+"F8.wireOp",EDGE,"E68.0")]}),-1.0]])],"derivedFrom":subQ0})])],"isStart":false})});}
            var Q24;
            {var subQ0=sQuery(id+"F8.wireOp",EDGE,"E39.0");Q24=makeQuery(id+"F9.boolean.opBoolean","COPY",EDGE,{"derivedFrom":makeQuery(id+"F9.opExtrude","CAP_EDGE",EDGE,{"disambiguationData":[OSD([subQ0]),TDD([makeQuery(id+"F8.imprint","IMPRINT",EDGE,{"disambiguationData":[TD([[makeQuery(id+"F8.imprint","INTERSECT",VERTEX,{"derivedFrom":[subQ0,sQuery(id+"F8.wireOp",EDGE,"E70.0")]}),-1.0]])],"derivedFrom":subQ0})])],"isStart":false})});}
            var Q25;
            {var subQ0=sQuery(id+"F8.wireOp",EDGE,"E39.0");Q25=makeQuery(id+"F9.boolean.opBoolean","COPY",EDGE,{"derivedFrom":makeQuery(id+"F9.opExtrude","CAP_EDGE",EDGE,{"disambiguationData":[OSD([subQ0]),TDD([makeQuery(id+"F8.imprint","IMPRINT",EDGE,{"disambiguationData":[TD([[makeQuery(id+"F8.imprint","INTERSECT",VERTEX,{"derivedFrom":[subQ0,sQuery(id+"F8.wireOp",EDGE,"E80.0")]}),-1.0]])],"derivedFrom":subQ0})])],"isStart":false})});}
            var Q26;
            {var subQ0=sQuery(id+"F8.wireOp",EDGE,"E39.0");Q26=makeQuery(id+"F9.boolean.opBoolean","COPY",EDGE,{"derivedFrom":makeQuery(id+"F9.opExtrude","CAP_EDGE",EDGE,{"disambiguationData":[OSD([subQ0]),TDD([makeQuery(id+"F8.imprint","IMPRINT",EDGE,{"disambiguationData":[TD([[makeQuery(id+"F8.imprint","INTERSECT",VERTEX,{"derivedFrom":[subQ0,sQuery(id+"F8.wireOp",EDGE,"E78.0")]}),-1.0]])],"derivedFrom":subQ0})])],"isStart":false})});}
            var Q27;
            {var subQ0=sQuery(id+"F8.wireOp",EDGE,"E39.0");Q27=makeQuery(id+"F9.boolean.opBoolean","COPY",EDGE,{"derivedFrom":makeQuery(id+"F9.opExtrude","CAP_EDGE",EDGE,{"disambiguationData":[OSD([subQ0]),TDD([makeQuery(id+"F8.imprint","IMPRINT",EDGE,{"disambiguationData":[TD([[makeQuery(id+"F8.imprint","INTERSECT",VERTEX,{"derivedFrom":[subQ0,sQuery(id+"F8.wireOp",EDGE,"E76.0")]}),-1.0]])],"derivedFrom":subQ0})])],"isStart":false})});}
            var Q28;
            {var subQ0=sQuery(id+"F8.wireOp",EDGE,"E39.0");Q28=makeQuery(id+"F9.boolean.opBoolean","COPY",EDGE,{"derivedFrom":makeQuery(id+"F9.opExtrude","CAP_EDGE",EDGE,{"disambiguationData":[OSD([subQ0]),TDD([makeQuery(id+"F8.imprint","IMPRINT",EDGE,{"disambiguationData":[TD([[makeQuery(id+"F8.imprint","INTERSECT",VERTEX,{"derivedFrom":[subQ0,sQuery(id+"F8.wireOp",EDGE,"E74.0")]}),-1.0]])],"derivedFrom":subQ0})])],"isStart":false})});}
            var Q29;
            {var subQ0=sQuery(id+"F8.wireOp",EDGE,"E39.0");Q29=makeQuery(id+"F9.boolean.opBoolean","COPY",EDGE,{"derivedFrom":makeQuery(id+"F9.opExtrude","CAP_EDGE",EDGE,{"disambiguationData":[OSD([subQ0]),TDD([makeQuery(id+"F8.imprint","IMPRINT",EDGE,{"disambiguationData":[TD([[makeQuery(id+"F8.imprint","INTERSECT",VERTEX,{"derivedFrom":[subQ0,sQuery(id+"F8.wireOp",EDGE,"E72.0")]}),-1.0]])],"derivedFrom":subQ0})])],"isStart":false})});}
            chamfer(context, id + "F10", {"entities" : qUnion([Q0, Q1, Q2, Q3, Q4, Q5, Q6, Q7, Q8, Q9, Q10, Q11, Q12, Q13, Q14, Q15, Q16, Q17, Q18, Q19, Q20, Q21, Q22, Q23, Q24, Q25, Q26, Q27, Q28, Q29]), "width" : 0.8 * mm, "tangentPropagation" : true});
        }
    });
